# Revit family: Dallmeier_Panomera_S-Series
name_source: partatom
category: Sicherheitsgeräte
units: mm (PartAtom-declared; Revit-internal decimal feet)

## family parameters
Basisbauteil = Fläche
Beim Laden mit Abzugskörper schneiden = Nein
Bemaßung runder Anschluss = Durchmesser verwenden
Beschriftungsausrichtung beibehalten = Nein
Gemeinsam genutzt = Nein
Raumberechnungspunkt = Nein
Teiletyp = Normal

## types (9) — shared parameters
Hersteller = Dallmeier electronic GmbH
URL = https://www.dallmeier.com
dimensions = 348x183x441mm
operating temperature = -40°C to +60°C
recommended network bandwidth = 1000 Mbps
voltage supply = 48 V

## per-type parameters (varying)
| type | FOV horizontal | FOV vertical | Modul_FOV_Horizontal | Pixel horizontal | Vorgabe-Ansicht | aspect ratio | installation height | number of sensor pixel | number of sensors | power consumption | required network bandwidth | weight |
| Panomera S8 Ultraline 190/30 | 30,00° | 52,00° | 10,34° | 3610 | 121,5 cm | 3:5 | 4,5 - 9 m | 96 MP | 8 | 100 W | 128 Mbps | 17,50 kg |
| Panomera S8 Ultraline 184/45 | 45,00° | 77,00° | 15,73° | 3610 | 121,9 cm | 3:5 | 4,5 - 9 m | 96 MP | 8 | 100 W | 128 Mbps | 17,50 kg |
| Panomera S8 Ultraline 78/75 | 75,00° | 30,00° | 19,83° | 3610 | 121,9 cm | 5:2 | 4,5 - 10 m | 96 MP | 8 | 100 W | 128 Mbps | 17,50 kg |
| Panomera S8 Topline 178/22 | 22,00° | 62,00° | 7,71° | 2720 | 121,9 cm | 3:8 | 4,5 - 9,5 m | 51 MP | 8 | 100 W | 48 Mbps | 17,50 kg |
| Panomera S8 Topline 115/30 | 30,00° | 52,00° | 10,13° | 2720 | 121,9 cm | 3:5 | 4,5 - 10 m | 51 MP | 8 | 100 W | 48 Mbps | 17,50 kg |
| Panomera S8 Topline 87/45 | 45,00° | 60,00° | 15,35° | 2720 | 121,9 cm | 3:4 | 4,5 - 9 m | 51 MP | 8 | 100 W | 48 Mbps | 17,50 kg |
| Panomera S8 Topline 43/90 | 90,00° | 33,00° | 22,72° | 2720 | 121,9 cm | 11:4 | 4,5 - 10 m | 51 MP | 8 | 100 W | 48 Mbps | 17,50 kg |
| Panomera S4 Topline 46/15 | 15,00° | 24,00° | 7,71° | 2720 | 121,9 cm | 3:5 | 4.5 m to 6 m | 25 MP | 4 | 0 W | 24 Mbps | 16,00 kg |
| Panomera S4 Topline 46/30 | 30,00° | 46,00° | 7,71° | 2720 | 121,9 cm | 3:5 | 4,5 - 6 m | 25 MP | 4 | 70 W | 24 Mbps | 16,00 kg |

note: column(s) folded — value = type name in every type: Modell

## geometry (parser evidence)
native form markers: Sweep x25
no freeform markers — native parametric forms only
